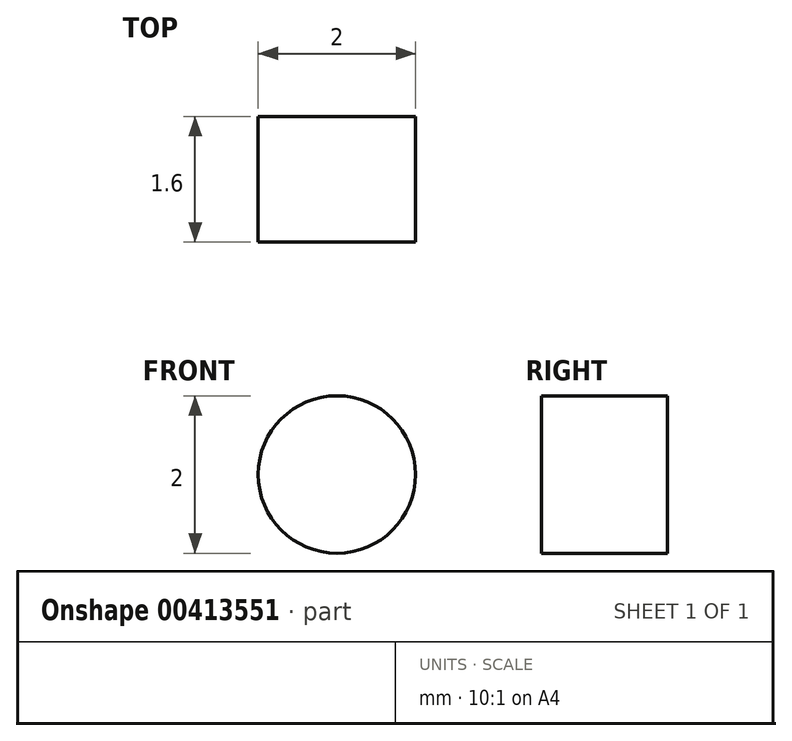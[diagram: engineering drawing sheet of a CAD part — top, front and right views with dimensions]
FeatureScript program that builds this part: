
annotation { "Feature Type Name" : "Feature", "Feature Type Description" : "" }
export const myFeature = defineFeature(function(context is Context, id is Id, definition is map)
    precondition{}
    {
        {
            var Q0;
            Q0=qCreatedBy(makeId("Front.planeOp"),FACE);
            var sketch = newSketch(context, id + "F0", { "sketchPlane" : qUnion([Q0])});
            skLineSegment(sketch, "E0.bottom", {"start": v(17, 4) * mm, "end": v(-17, 4) * mm});
            skLineSegment(sketch, "E0.top", {"start": v(17, -4) * mm, "end": v(-17, -4) * mm});
            skLineSegment(sketch, "E0.left", {"start": v(17, 4) * mm, "end": v(17, -4) * mm});
            skLineSegment(sketch, "E0.right", {"start": v(-17, 4) * mm, "end": v(-17, -4) * mm});
            skPoint(sketch, "E0.middle", {"position": v(0, 0) * mm});
            skSolve(sketch);
        }
        {
            var Q0;
            Q0=makeQuery(id+"F0.imprint","IMPRINT",FACE,{"disambiguationData":[TD([[makeQuery(id+"F0.imprint","IMPRINT",EDGE,{"derivedFrom":sQuery(id+"F0.wireOp",EDGE,"E0.bottom")}),1.0]])]});
            extrude(context, id + "F1", {"entities" : qUnion([Q0]), "depth" : 1.6 * mm});
        }
        {
            var Q0;
            Q0=makeQuery(id+"F1.opExtrude","CAP_FACE",FACE,{"disambiguationData":[OSD([sQuery(id+"F0.wireOp",EDGE,"E0.bottom"),sQuery(id+"F0.wireOp",EDGE,"E0.top"),sQuery(id+"F0.wireOp",EDGE,"E0.left"),sQuery(id+"F0.wireOp",EDGE,"E0.right")])],"isStart":false});
            var sketch = newSketch(context, id + "F2", { "sketchPlane" : qUnion([Q0])});
            skCircle(sketch, "E1", {"center": v(-15, 0) * mm, "radius": 1 * mm});
            skCircle(sketch, "E2.MirrorC", {"center": v(15, 0) * mm, "radius": 1 * mm});
            skSolve(sketch);
        }
        {
            var Q0;
            Q0=makeQuery(id+"F2.imprint","IMPRINT",FACE,{"disambiguationData":[TD([[makeQuery(id+"F2.imprint","IMPRINT",EDGE,{"derivedFrom":sQuery(id+"F2.wireOp",EDGE,"E1")}),1.0]])]});
            var Q1;
            Q1=makeQuery(id+"F2.imprint","IMPRINT",FACE,{"disambiguationData":[TD([[makeQuery(id+"F2.imprint","IMPRINT",EDGE,{"derivedFrom":sQuery(id+"F2.wireOp",EDGE,"E2.MirrorC")}),-1.0]])]});
            var Q2;
            Q2=sQuery(id+"F2.wireOp",EDGE,"E1");
            extrude(context, id + "F3", {"entities" : qUnion([Q0, Q1]), "operationType" : NewBodyOperationType.REMOVE, "surfaceEntities" : qUnion([Q2]), "endBound" : BoundingType.THROUGH_ALL, "oppositeDirection" : true, "depth" : 25 * mm});
        }
    });
